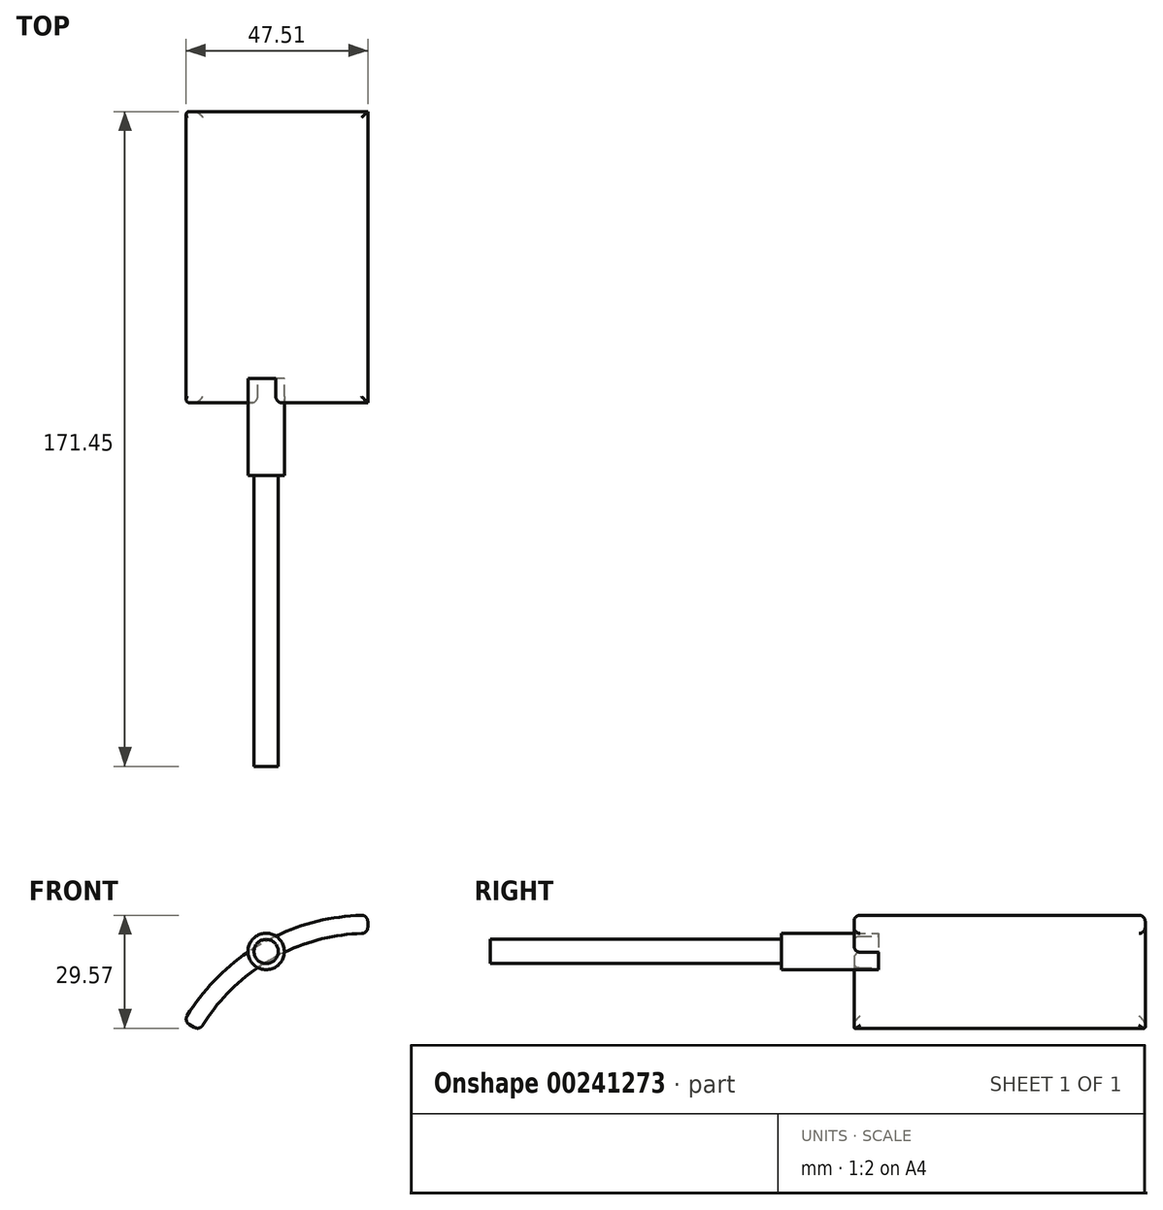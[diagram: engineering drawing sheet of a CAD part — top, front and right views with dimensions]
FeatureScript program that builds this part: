
annotation { "Feature Type Name" : "Feature", "Feature Type Description" : "" }
export const myFeature = defineFeature(function(context is Context, id is Id, definition is map)
    precondition{}
    {
        {
            var Q0;
            Q0=qCreatedBy(makeId("Front.planeOp"),FACE);
            var sketch = newSketch(context, id + "F0", { "sketchPlane" : qUnion([Q0])});
            skArc(sketch, "E0", {"start": v(0, 55.56) * mm, "mid": v(-27.78, 48.12) * mm, "end": v(-48.12, 27.78) * mm});
            skArc(sketch, "E1", {"start": v(0, 50.8) * mm, "mid": v(-25.4, 44) * mm, "end": v(-44, 25.4) * mm});
            skLineSegment(sketch, "E2", {"start": v(0, 0) * mm, "end": v(0, 76.23) * mm, "construction": true});
            skLineSegment(sketch, "E3", {"start": v(0, 0) * mm, "end": v(-51.6, 29.8) * mm, "construction": true});
            skLineSegment(sketch, "E4", {"start": v(-48.12, 27.78) * mm, "end": v(-44, 25.4) * mm});
            skLineSegment(sketch, "E5", {"start": v(0, 55.56) * mm, "end": v(0, 50.8) * mm});
            skSolve(sketch);
        }
        {
            var Q0;
            Q0 = qSketchRegion(id + "F0", true);
            extrude(context, id + "F1", {"entities" : qUnion([Q0]), "depth" : 76.2 * mm});
        }
        {
            var Q0;
            Q0=makeQuery(id+"F1.opExtrude","CAP_FACE",FACE,{"disambiguationData":[OSD([sQuery(id+"F0.wireOp",EDGE,"E0"),sQuery(id+"F0.wireOp",EDGE,"E1"),sQuery(id+"F0.wireOp",EDGE,"E4"),sQuery(id+"F0.wireOp",EDGE,"E5")])],"isStart":false});
            var sketch = newSketch(context, id + "F2", { "sketchPlane" : qUnion([Q0])});
            skLineSegment(sketch, "E6", {"start": v(0, 0) * mm, "end": v(0, 53.18) * mm, "construction": true});
            skLineSegment(sketch, "E7", {"start": v(0, 0) * mm, "end": v(-26.6, 46.06) * mm, "construction": true});
            skCircle(sketch, "E8", {"center": v(-26.6, 46.06) * mm, "radius": 4.76 * mm});
            skSolve(sketch);
        }
        {
            var Q0;
            Q0 = qSketchRegion(id + "F2", true);
            extrude(context, id + "F3", {"entities" : qUnion([Q0]), "operationType" : NewBodyOperationType.ADD, "endBound" : BoundingType.SYMMETRIC, "depth" : 12.7 * mm});
        }
        {
            var Q0;
            Q0=makeQuery(id+"F3.opExtrude","CAP_FACE",FACE,{"disambiguationData":[OSD([sQuery(id+"F2.wireOp",EDGE,"E8")])],"isStart":false});
            var sketch = newSketch(context, id + "F4", { "sketchPlane" : qUnion([Q0])});
            skCircle(sketch, "E9.0.0", {"center": v(-26.6, 46.06) * mm, "radius": 4.76 * mm});
            skSolve(sketch);
        }
        {
            var Q0;
            Q0 = qSketchRegion(id + "F4", true);
            extrude(context, id + "F5", {"entities" : qUnion([Q0]), "operationType" : NewBodyOperationType.ADD, "depth" : 12.7 * mm});
        }
        {
            var Q0;
            Q0=makeQuery(id+"F5.opExtrude","CAP_FACE",FACE,{"disambiguationData":[OSD([sQuery(id+"F4.wireOp",EDGE,"E9.0.0")])],"isStart":false});
            var sketch = newSketch(context, id + "F6", { "sketchPlane" : qUnion([Q0])});
            skCircle(sketch, "E10.0.0", {"center": v(-26.6, 46.06) * mm, "radius": 4.76 * mm});
            skCircle(sketch, "E11", {"center": v(-26.6, 46.06) * mm, "radius": 3.18 * mm});
            skSolve(sketch);
        }
        {
            var Q0;
            Q0=makeQuery(id+"F6.imprint","IMPRINT",FACE,{"disambiguationData":[TD([[makeQuery(id+"F6.imprint","IMPRINT",EDGE,{"derivedFrom":sQuery(id+"F6.wireOp",EDGE,"E11")}),1.0]])]});
            extrude(context, id + "F7", {"entities" : qUnion([Q0]), "operationType" : NewBodyOperationType.ADD, "depth" : 76.2 * mm});
        }
        {
            var Q0;
            Q0=makeQuery(id+"F1.opExtrude","SWEPT_EDGE",EDGE,{"disambiguationData":[OSD([sQuery(id+"F0.wireOp",EDGE,"E0"),sQuery(id+"F0.wireOp",EDGE,"E4")])]});
            var Q1;
            Q1=makeQuery(id+"F1.opExtrude","SWEPT_EDGE",EDGE,{"disambiguationData":[OSD([sQuery(id+"F0.wireOp",EDGE,"E1"),sQuery(id+"F0.wireOp",EDGE,"E4")])]});
            var Q2;
            {var subQ0=sQuery(id+"F0.wireOp",EDGE,"E0");var subQ1=sQuery(id+"F0.wireOp",EDGE,"E4");Q2=makeQuery(id+"F3.boolean.opBoolean","SPLIT",EDGE,{"disambiguationData":[TD([makeQuery(id+"F1.opExtrude","SWEPT_FACE",FACE,{"disambiguationData":[OSD([subQ1])]})])],"derivedFrom":makeQuery(id+"F1.opExtrude","CAP_EDGE",EDGE,{"disambiguationData":[OSD([subQ0])],"isStart":false})});}
            var Q3;
            {var subQ0=sQuery(id+"F0.wireOp",EDGE,"E4");var subQ1=sQuery(id+"F0.wireOp",EDGE,"E1");Q3=makeQuery(id+"F3.boolean.opBoolean","SPLIT",EDGE,{"disambiguationData":[TD([makeQuery(id+"F1.opExtrude","SWEPT_FACE",FACE,{"disambiguationData":[OSD([subQ0])]})])],"derivedFrom":makeQuery(id+"F1.opExtrude","CAP_EDGE",EDGE,{"disambiguationData":[OSD([subQ1])],"isStart":false})});}
            var Q4;
            {var subQ0=sQuery(id+"F0.wireOp",EDGE,"E0");var subQ1=sQuery(id+"F0.wireOp",EDGE,"E5");Q4=makeQuery(id+"F3.boolean.opBoolean","SPLIT",EDGE,{"disambiguationData":[TD([makeQuery(id+"F1.opExtrude","SWEPT_FACE",FACE,{"disambiguationData":[OSD([subQ1])]})])],"derivedFrom":makeQuery(id+"F1.opExtrude","CAP_EDGE",EDGE,{"disambiguationData":[OSD([subQ0])],"isStart":false})});}
            var Q5;
            {var subQ0=sQuery(id+"F0.wireOp",EDGE,"E5");var subQ1=sQuery(id+"F0.wireOp",EDGE,"E1");Q5=makeQuery(id+"F3.boolean.opBoolean","SPLIT",EDGE,{"disambiguationData":[TD([makeQuery(id+"F1.opExtrude","SWEPT_FACE",FACE,{"disambiguationData":[OSD([subQ0])]})])],"derivedFrom":makeQuery(id+"F1.opExtrude","CAP_EDGE",EDGE,{"disambiguationData":[OSD([subQ1])],"isStart":false})});}
            var Q6;
            Q6=makeQuery(id+"F1.opExtrude","SWEPT_EDGE",EDGE,{"disambiguationData":[OSD([sQuery(id+"F0.wireOp",EDGE,"E0"),sQuery(id+"F0.wireOp",EDGE,"E5")])]});
            var Q7;
            Q7=makeQuery(id+"F1.opExtrude","SWEPT_EDGE",EDGE,{"disambiguationData":[OSD([sQuery(id+"F0.wireOp",EDGE,"E1"),sQuery(id+"F0.wireOp",EDGE,"E5")])]});
            var Q8;
            Q8=makeQuery(id+"F1.opExtrude","CAP_EDGE",EDGE,{"disambiguationData":[OSD([sQuery(id+"F0.wireOp",EDGE,"E0")])],"isStart":true});
            var Q9;
            Q9=makeQuery(id+"F1.opExtrude","CAP_EDGE",EDGE,{"disambiguationData":[OSD([sQuery(id+"F0.wireOp",EDGE,"E1")])],"isStart":true});
            fillet(context, id + "F8", {"entities" : qUnion([Q0, Q1, Q2, Q3, Q4, Q5, Q6, Q7, Q8, Q9]), "radius" : 1.6 * mm, "tangentPropagation" : true, "allowEdgeOverflow" : false});
        }
    });
